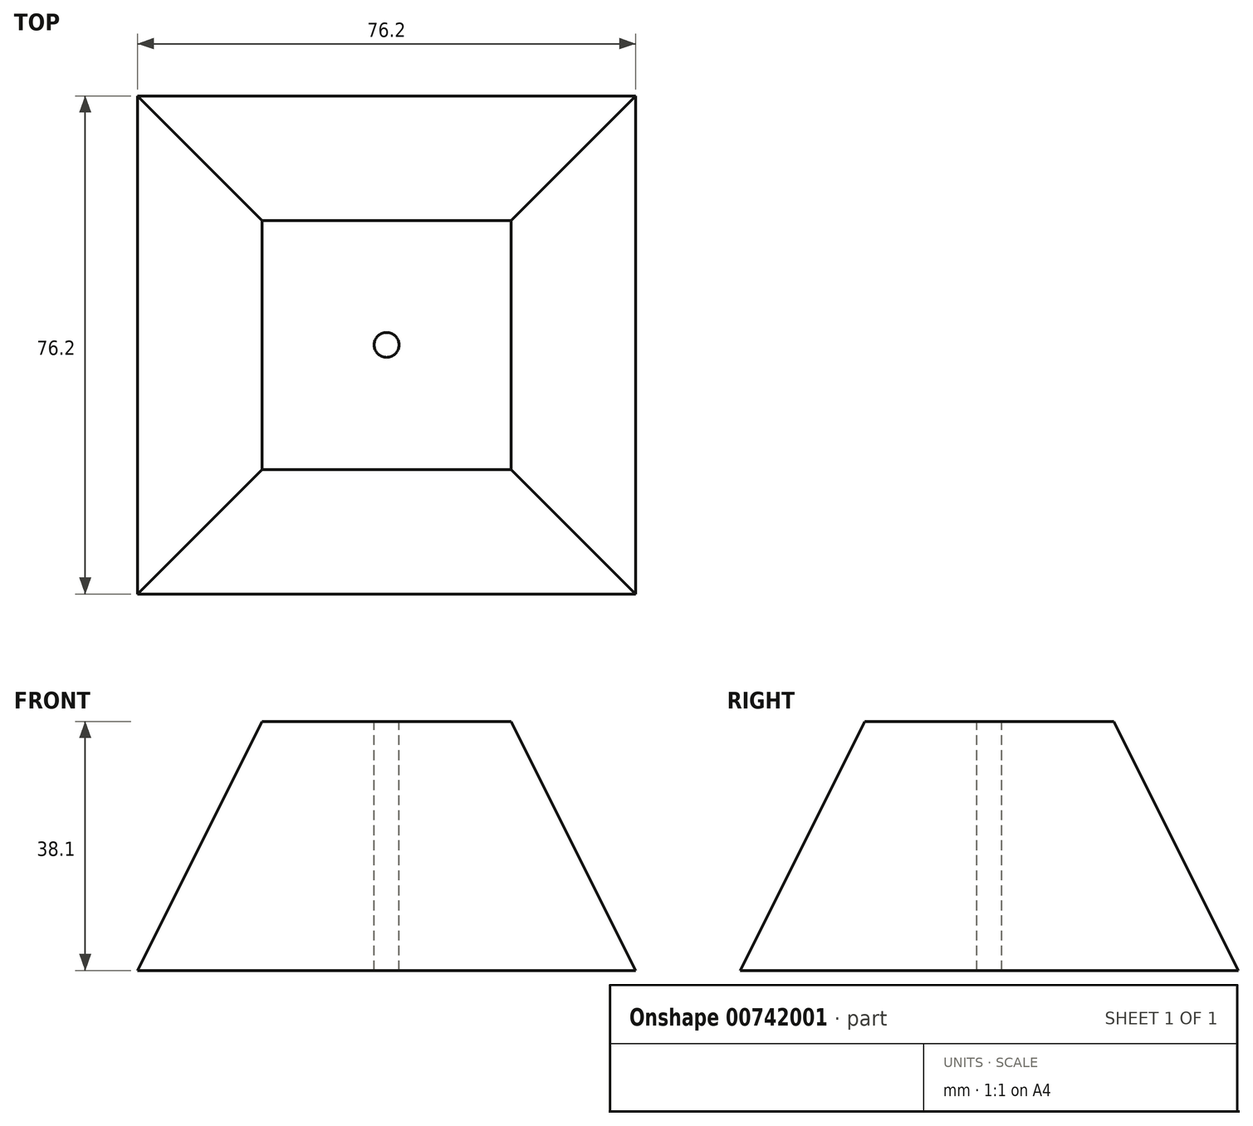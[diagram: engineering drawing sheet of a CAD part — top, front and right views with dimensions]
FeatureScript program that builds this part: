
annotation { "Feature Type Name" : "Feature", "Feature Type Description" : "" }
export const myFeature = defineFeature(function(context is Context, id is Id, definition is map)
    precondition{}
    {
        {
            var Q0;
            Q0=qCreatedBy(makeId("Top.planeOp"),FACE);
            var sketch = newSketch(context, id + "F0", { "sketchPlane" : qUnion([Q0])});
            skLineSegment(sketch, "E0.bottom", {"start": v(38.1, -38.1) * mm, "end": v(-38.1, -38.1) * mm});
            skLineSegment(sketch, "E0.top", {"start": v(38.1, 38.1) * mm, "end": v(-38.1, 38.1) * mm});
            skLineSegment(sketch, "E0.left", {"start": v(38.1, -38.1) * mm, "end": v(38.1, 38.1) * mm});
            skLineSegment(sketch, "E0.right", {"start": v(-38.1, -38.1) * mm, "end": v(-38.1, 38.1) * mm});
            skPoint(sketch, "E0.middle", {"position": v(0, 0) * mm});
            skSolve(sketch);
        }
        {
            var Q0;
            Q0=qCreatedBy(makeId("Top.planeOp"),FACE);
            cPlane(context, id + "F1", {"entities" : qUnion([Q0]), "cplaneType" : CPlaneType.OFFSET, "offset" : 38.1 * mm, "width" : 152.4 * mm, "height" : 152.4 * mm});
        }
        {
            var Q0;
            Q0=qCreatedBy(id+"F1.planeOp",FACE);
            var sketch = newSketch(context, id + "F2", { "sketchPlane" : qUnion([Q0])});
            skLineSegment(sketch, "E1.bottom", {"start": v(-19.05, 19.05) * mm, "end": v(19.05, 19.05) * mm});
            skLineSegment(sketch, "E1.top", {"start": v(-19.05, -19.05) * mm, "end": v(19.05, -19.05) * mm});
            skLineSegment(sketch, "E1.left", {"start": v(-19.05, 19.05) * mm, "end": v(-19.05, -19.05) * mm});
            skLineSegment(sketch, "E1.right", {"start": v(19.05, 19.05) * mm, "end": v(19.05, -19.05) * mm});
            skPoint(sketch, "E1.middle", {"position": v(0, 0) * mm});
            skSolve(sketch);
        }
        {
            var Q0;
            Q0=makeQuery(id+"F0.imprint","IMPRINT",FACE,{"disambiguationData":[TD([[makeQuery(id+"F0.imprint","IMPRINT",EDGE,{"derivedFrom":sQuery(id+"F0.wireOp",EDGE,"E0.bottom")}),-1.0]])]});
            var Q1;
            Q1=makeQuery(id+"F2.imprint","IMPRINT",FACE,{"disambiguationData":[TD([[makeQuery(id+"F2.imprint","IMPRINT",EDGE,{"derivedFrom":sQuery(id+"F2.wireOp",EDGE,"E1.bottom")}),-1.0]])]});
            var Q2;
            Q2=sQuery(id+"F2.wireOp",VERTEX,"E1.left.end");
            var Q3;
            Q3=sQuery(id+"F0.wireOp",VERTEX,"E0.right.start");
            var Q4;
            Q4=sQuery(id+"F2.wireOp",VERTEX,"E1.left.start");
            var Q5;
            Q5=sQuery(id+"F0.wireOp",VERTEX,"E0.right.end");
            var Q6;
            Q6=sQuery(id+"F2.wireOp",VERTEX,"E1.right.start");
            var Q7;
            Q7=sQuery(id+"F0.wireOp",VERTEX,"E0.left.end");
            var Q8;
            Q8=sQuery(id+"F2.wireOp",VERTEX,"E1.top.end");
            var Q9;
            Q9=sQuery(id+"F0.wireOp",VERTEX,"E0.left.start");
            loft(context, id + "F3", {"sheetProfilesArray" : [{ "sheetProfileEntities" : qUnion([Q0]) }, { "sheetProfileEntities" : qUnion([Q1]) }], "connections" : [{ "connectionEntities" : qUnion([Q2, Q3, Q4, Q5, Q6, Q7, Q8, Q9]), "connectionEdgeQueries" : qUnion([]), "connectionEdgeParameters" : [] }]});
        }
        {
            var Q0;
            Q0=qCreatedBy(id+"F1.planeOp",FACE);
            var sketch = newSketch(context, id + "F4", { "sketchPlane" : qUnion([Q0])});
            skLineSegment(sketch, "E2.bottom", {"start": v(19.05, -19.05) * mm, "end": v(-19.05, -19.05) * mm});
            skLineSegment(sketch, "E2.top", {"start": v(19.05, 19.05) * mm, "end": v(-19.05, 19.05) * mm});
            skLineSegment(sketch, "E2.left", {"start": v(19.05, -19.05) * mm, "end": v(19.05, 19.05) * mm});
            skLineSegment(sketch, "E2.right", {"start": v(-19.05, -19.05) * mm, "end": v(-19.05, 19.05) * mm});
            skPoint(sketch, "E2.middle", {"position": v(0, 0) * mm});
            skSolve(sketch);
        }
        {
            var Q0;
            Q0=qCreatedBy(makeId("Front.planeOp"),FACE);
            var sketch = newSketch(context, id + "F5", { "sketchPlane" : qUnion([Q0])});
            skLineSegment(sketch, "E3", {"start": v(0, 38.48) * mm, "end": v(0, 76.58) * mm});
            skSolve(sketch);
        }
        {
            var Q0;
            Q0=makeQuery(id+"F4.imprint","IMPRINT",FACE,{"disambiguationData":[TD([[makeQuery(id+"F4.imprint","IMPRINT",EDGE,{"derivedFrom":sQuery(id+"F4.wireOp",EDGE,"E2.bottom")}),-1.0]])]});
            var Q1;
            Q1=sQuery(id+"F5.wireOp",VERTEX,"E3.end");
            loft(context, id + "F6", {"sheetProfilesArray" : [{ "sheetProfileEntities" : qUnion([Q0]) }, { "sheetProfileEntities" : qUnion([Q1]) }]});
        }
        {
            var Q0;
            Q0=qCreatedBy(id+"F1.planeOp",FACE);
            var sketch = newSketch(context, id + "F7", { "sketchPlane" : qUnion([Q0])});
            skPoint(sketch, "E4", {"position": v(0, 0) * mm});
            skSolve(sketch);
        }
        {
            var Q0;
            Q0=sQuery(id+"F7.wireOp",VERTEX,"E4");
            var Q1;
            Q1=makeQuery(id+"F6.opLoft","SWEPT_BODY",BODY,{"disambiguationData":[OSD([makeQuery(id+"F4.imprint","IMPRINT",FACE,{"disambiguationData":[TD([[makeQuery(id+"F4.imprint","IMPRINT",EDGE,{"derivedFrom":sQuery(id+"F4.wireOp",EDGE,"E2.bottom")}),-1.0]])]}),sQuery(id+"F5.wireOp",VERTEX,"E3.end")])]});
            hole(context, id + "F8", {"style" : HoleStyle.SIMPLE, "endStyle" : HoleEndStyle.THROUGH, "oppositeDirection" : true, "holeDiameter" : 3.8 * mm, "majorDiameter" : 6.35 * mm, "isTappedThrough" : true, "tappedDepth" : 12.7 * mm, "tapClearance" : 3, "locations" : qUnion([Q0]), "scope" : qUnion([Q1])});
        }
        {
            var Q0;
            Q0=makeQuery(id+"F3.opLoft","CAP_FACE",FACE,{"disambiguationData":[OSD([makeQuery(id+"F2.imprint","IMPRINT",FACE,{"disambiguationData":[TD([[makeQuery(id+"F2.imprint","IMPRINT",EDGE,{"derivedFrom":sQuery(id+"F2.wireOp",EDGE,"E1.bottom")}),-1.0]])]})])],"isStart":true});
            var sketch = newSketch(context, id + "F9", { "sketchPlane" : qUnion([Q0])});
            skPoint(sketch, "E5", {"position": v(0, 0) * mm});
            skSolve(sketch);
        }
        {
            var Q0;
            Q0=sQuery(id+"F9.wireOp",VERTEX,"E5");
            var Q1;
            Q1=makeQuery(id+"F3.opLoft","SWEPT_BODY",BODY,{"disambiguationData":[OSD([makeQuery(id+"F0.imprint","IMPRINT",FACE,{"disambiguationData":[TD([[makeQuery(id+"F0.imprint","IMPRINT",EDGE,{"derivedFrom":sQuery(id+"F0.wireOp",EDGE,"E0.bottom")}),-1.0]])]}),makeQuery(id+"F2.imprint","IMPRINT",FACE,{"disambiguationData":[TD([[makeQuery(id+"F2.imprint","IMPRINT",EDGE,{"derivedFrom":sQuery(id+"F2.wireOp",EDGE,"E1.bottom")}),-1.0]])]})])]});
            hole(context, id + "F10", {"style" : HoleStyle.SIMPLE, "endStyle" : HoleEndStyle.THROUGH, "holeDiameter" : 3.8 * mm, "majorDiameter" : 6.35 * mm, "isTappedThrough" : true, "tappedDepth" : 12.7 * mm, "tapClearance" : 3, "locations" : qUnion([Q0]), "scope" : qUnion([Q1])});
        }
        {
            var Q0;
            Q0=makeQuery(id+"F6.opLoft","SWEPT_BODY",BODY,{"disambiguationData":[OSD([makeQuery(id+"F4.imprint","IMPRINT",FACE,{"disambiguationData":[TD([[makeQuery(id+"F4.imprint","IMPRINT",EDGE,{"derivedFrom":sQuery(id+"F4.wireOp",EDGE,"E2.bottom")}),-1.0]])]}),sQuery(id+"F5.wireOp",VERTEX,"E3.end")])]});
            deleteBodies(context, id + "F11", {"entities" : qUnion([Q0])});
        }
    });
